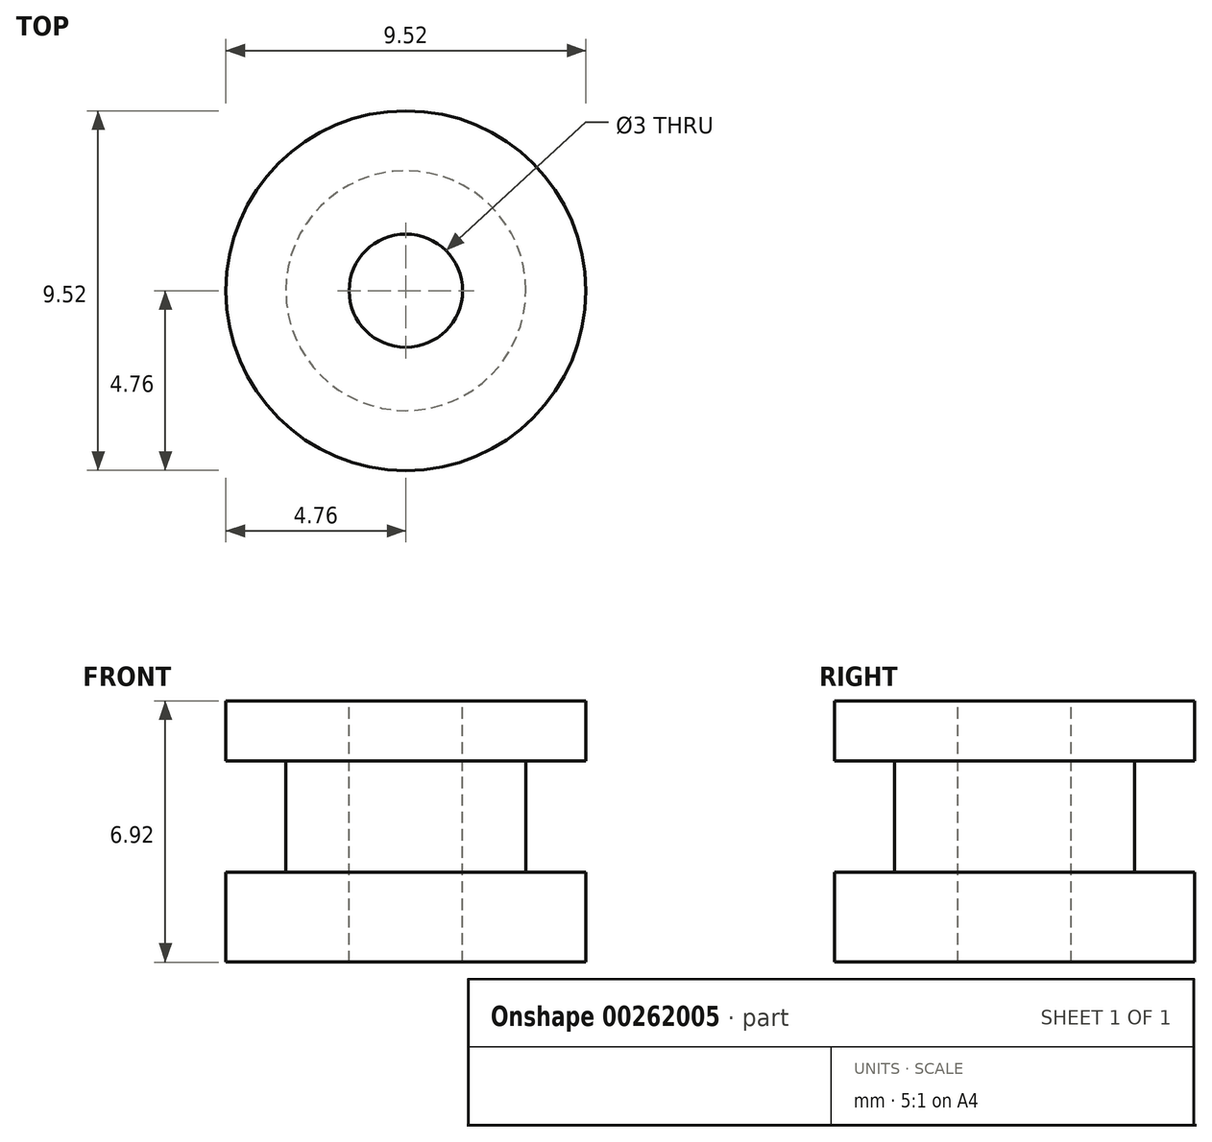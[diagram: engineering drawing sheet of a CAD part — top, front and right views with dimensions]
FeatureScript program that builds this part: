
annotation { "Feature Type Name" : "Feature", "Feature Type Description" : "" }
export const myFeature = defineFeature(function(context is Context, id is Id, definition is map)
    precondition{}
    {
        {
            var Q0;
            Q0=qCreatedBy(makeId("Front.planeOp"),FACE);
            var sketch = newSketch(context, id + "F0", { "sketchPlane" : qUnion([Q0])});
            skLineSegment(sketch, "E0", {"start": v(0, 12.22) * mm, "end": v(0, -12.17) * mm, "construction": true});
            skLineSegment(sketch, "E1", {"start": v(-1.5, 3.46) * mm, "end": v(-1.5, -3.46) * mm});
            skLineSegment(sketch, "E2", {"start": v(-1.5, -3.46) * mm, "end": v(-4.76, -3.46) * mm});
            skLineSegment(sketch, "E3", {"start": v(-4.76, -3.46) * mm, "end": v(-4.76, -1.07) * mm});
            skLineSegment(sketch, "E4", {"start": v(-4.76, -1.08) * mm, "end": v(-3.17, -1.08) * mm});
            skLineSegment(sketch, "E5", {"start": v(-3.17, -1.08) * mm, "end": v(-3.17, 1.86) * mm});
            skLineSegment(sketch, "E6", {"start": v(-3.17, 1.86) * mm, "end": v(-4.76, 1.86) * mm});
            skLineSegment(sketch, "E7", {"start": v(-4.76, 1.86) * mm, "end": v(-4.76, 3.46) * mm});
            skLineSegment(sketch, "E8", {"start": v(-4.76, 3.46) * mm, "end": v(-1.5, 3.46) * mm});
            skPoint(sketch, "E9", {"position": v(-1.5, 0) * mm});
            skPoint(sketch, "E9.positionSnap0", {"position": v(-1.5, 0) * mm});
            skSolve(sketch);
        }
        {
            var Q0;
            Q0=makeQuery(id+"F0.imprint","IMPRINT",FACE,{"disambiguationData":[TD([[makeQuery(id+"F0.imprint","IMPRINT",EDGE,{"derivedFrom":sQuery(id+"F0.wireOp",EDGE,"E1")}),-1.0]])]});
            var Q1;
            Q1=sQuery(id+"F0.wireOp",EDGE,"E0");
            revolve(context, id + "F1", {"entities" : qUnion([Q0]), "axis" : qUnion([Q1]), "revolveType" : RevolveType.FULL});
        }
    });
